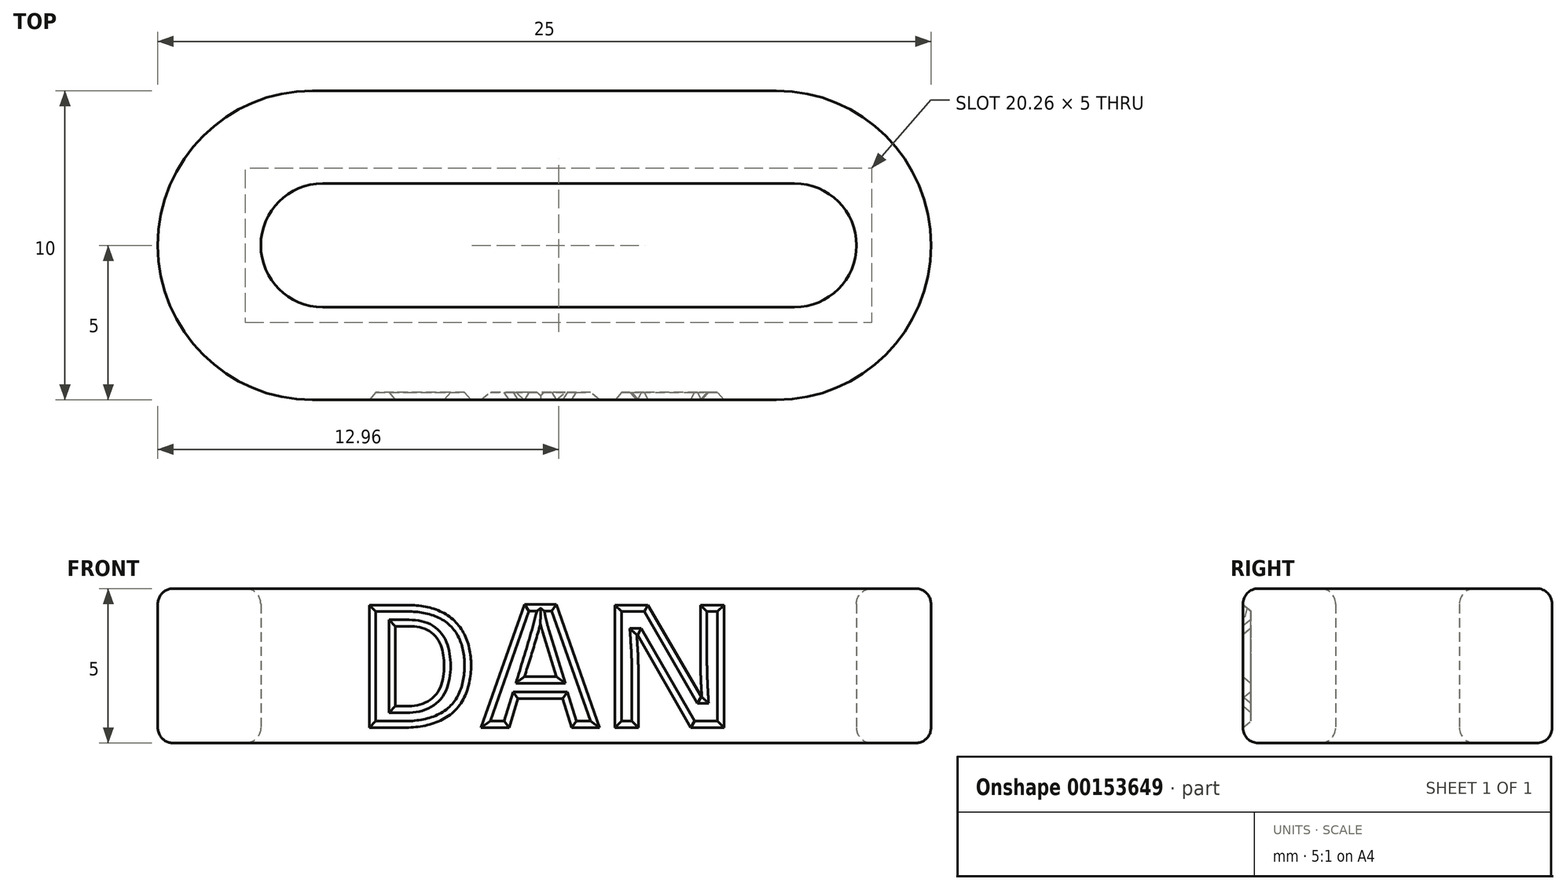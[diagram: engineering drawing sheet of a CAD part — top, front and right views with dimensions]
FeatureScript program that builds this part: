
annotation { "Feature Type Name" : "Feature", "Feature Type Description" : "" }
export const myFeature = defineFeature(function(context is Context, id is Id, definition is map)
    precondition{}
    {
        {
            var Q0;
            Q0=qCreatedBy(makeId("Top.planeOp"),FACE);
            var sketch = newSketch(context, id + "F0", { "sketchPlane" : qUnion([Q0])});
            skLineSegment(sketch, "E0.bottom", {"start": v(12.5, -5) * mm, "end": v(-12.5, -5) * mm});
            skLineSegment(sketch, "E0.top", {"start": v(12.5, 5) * mm, "end": v(-12.5, 5) * mm});
            skLineSegment(sketch, "E0.left", {"start": v(12.5, -5) * mm, "end": v(12.5, 5) * mm});
            skLineSegment(sketch, "E0.right", {"start": v(-12.5, -5) * mm, "end": v(-12.5, 5) * mm});
            skPoint(sketch, "E0.middle", {"position": v(0, 0) * mm});
            skArc(sketch, "E1", {"start": v(-7.17, 2) * mm, "mid": v(-9.17, 0) * mm, "end": v(-7.17, -2) * mm});
            skArc(sketch, "E2", {"start": v(8.09, -2) * mm, "mid": v(10.09, 0) * mm, "end": v(8.09, 2) * mm});
            skLineSegment(sketch, "E3", {"start": v(-7.17, 2) * mm, "end": v(8.09, 2) * mm});
            skLineSegment(sketch, "E4", {"start": v(8.09, -2) * mm, "end": v(-7.17, -2) * mm});
            skSolve(sketch);
        }
        {
            var Q0;
            Q0=makeQuery(id+"F0.imprint","IMPRINT",FACE,{"disambiguationData":[TD([[makeQuery(id+"F0.imprint","IMPRINT",EDGE,{"derivedFrom":sQuery(id+"F0.wireOp",EDGE,"E0.bottom")}),-1.0]])]});
            extrude(context, id + "F1", {"entities" : qUnion([Q0]), "depth" : 5 * mm});
        }
        {
            var Q0;
            Q0=makeQuery(id+"F1.opExtrude","SWEPT_EDGE",EDGE,{"disambiguationData":[OSD([sQuery(id+"F0.wireOp",EDGE,"E0.bottom"),sQuery(id+"F0.wireOp",EDGE,"E0.right")])]});
            var Q1;
            Q1=makeQuery(id+"F1.opExtrude","SWEPT_EDGE",EDGE,{"disambiguationData":[OSD([sQuery(id+"F0.wireOp",EDGE,"E0.bottom"),sQuery(id+"F0.wireOp",EDGE,"E0.left")])]});
            var Q2;
            Q2=makeQuery(id+"F1.opExtrude","SWEPT_EDGE",EDGE,{"disambiguationData":[OSD([sQuery(id+"F0.wireOp",EDGE,"E0.top"),sQuery(id+"F0.wireOp",EDGE,"E0.left")])]});
            var Q3;
            Q3=makeQuery(id+"F1.opExtrude","SWEPT_EDGE",EDGE,{"disambiguationData":[OSD([sQuery(id+"F0.wireOp",EDGE,"E0.top"),sQuery(id+"F0.wireOp",EDGE,"E0.right")])]});
            fillet(context, id + "F2", {"entities" : qUnion([Q0, Q1, Q2, Q3]), "radius" : 5 * mm, "tangentPropagation" : true, "allowEdgeOverflow" : false});
        }
        {
            var Q0;
            Q0=makeQuery(id+"F1.opExtrude","CAP_FACE",FACE,{"disambiguationData":[OSD([sQuery(id+"F0.wireOp",EDGE,"E0.bottom"),sQuery(id+"F0.wireOp",EDGE,"E0.top"),sQuery(id+"F0.wireOp",EDGE,"E0.left"),sQuery(id+"F0.wireOp",EDGE,"E0.right"),sQuery(id+"F0.wireOp",EDGE,"E1"),sQuery(id+"F0.wireOp",EDGE,"E2"),sQuery(id+"F0.wireOp",EDGE,"E3"),sQuery(id+"F0.wireOp",EDGE,"E4")])],"isStart":false});
            var Q1;
            Q1=makeQuery(id+"F1.opExtrude","CAP_FACE",FACE,{"disambiguationData":[OSD([sQuery(id+"F0.wireOp",EDGE,"E0.bottom"),sQuery(id+"F0.wireOp",EDGE,"E0.top"),sQuery(id+"F0.wireOp",EDGE,"E0.left"),sQuery(id+"F0.wireOp",EDGE,"E0.right"),sQuery(id+"F0.wireOp",EDGE,"E1"),sQuery(id+"F0.wireOp",EDGE,"E2"),sQuery(id+"F0.wireOp",EDGE,"E3"),sQuery(id+"F0.wireOp",EDGE,"E4")])],"isStart":true});
            fillet(context, id + "F3", {"entities" : qUnion([Q0, Q1]), "radius" : .5 * mm, "tangentPropagation" : true, "allowEdgeOverflow" : false});
        }
        {
            var Q0;
            Q0=makeQuery(id+"F1.opExtrude","SWEPT_FACE",FACE,{"disambiguationData":[OSD([sQuery(id+"F0.wireOp",EDGE,"E0.bottom")])]});
            var sketch = newSketch(context, id + "F4", { "sketchPlane" : qUnion([Q0])});
            skText(sketch, "E5", { "text": "DAN", "fontName": "OpenSans-Bold.ttf"});
            const initialGuessF4  = {"E5": [-0.00616, 0.0005, 1, 0, 0.004]};
            skSetInitialGuess(sketch, initialGuessF4);
            skSolve(sketch);
        }
        {
            var Q0;
            Q0=makeQuery(id+"F4.imprint","IMPRINT",FACE,{"disambiguationData":[TD([[makeQuery(id+"F4.imprint","IMPRINT",EDGE,{"derivedFrom":sQuery(id+"F4.wireOp",EDGE,"E5.sketch_text.stroke-0")}),-1.0]])]});
            var Q1;
            Q1=makeQuery(id+"F4.imprint","IMPRINT",FACE,{"disambiguationData":[TD([[makeQuery(id+"F4.imprint","IMPRINT",EDGE,{"derivedFrom":sQuery(id+"F4.wireOp",EDGE,"E5.sketch_text.stroke-12")}),-1.0]])]});
            var Q2;
            Q2=makeQuery(id+"F4.imprint","IMPRINT",FACE,{"disambiguationData":[TD([[makeQuery(id+"F4.imprint","IMPRINT",EDGE,{"derivedFrom":sQuery(id+"F4.wireOp",EDGE,"E5.sketch_text.stroke-24")}),1.0]])]});
            extrude(context, id + "F5", {"entities" : qUnion([Q0, Q1, Q2]), "operationType" : NewBodyOperationType.REMOVE, "oppositeDirection" : true, "depth" : .25 * mm, "hasDraft" : true, "draftAngle" : 40 * degree, "draftPullDirection" : true});
        }
    });
